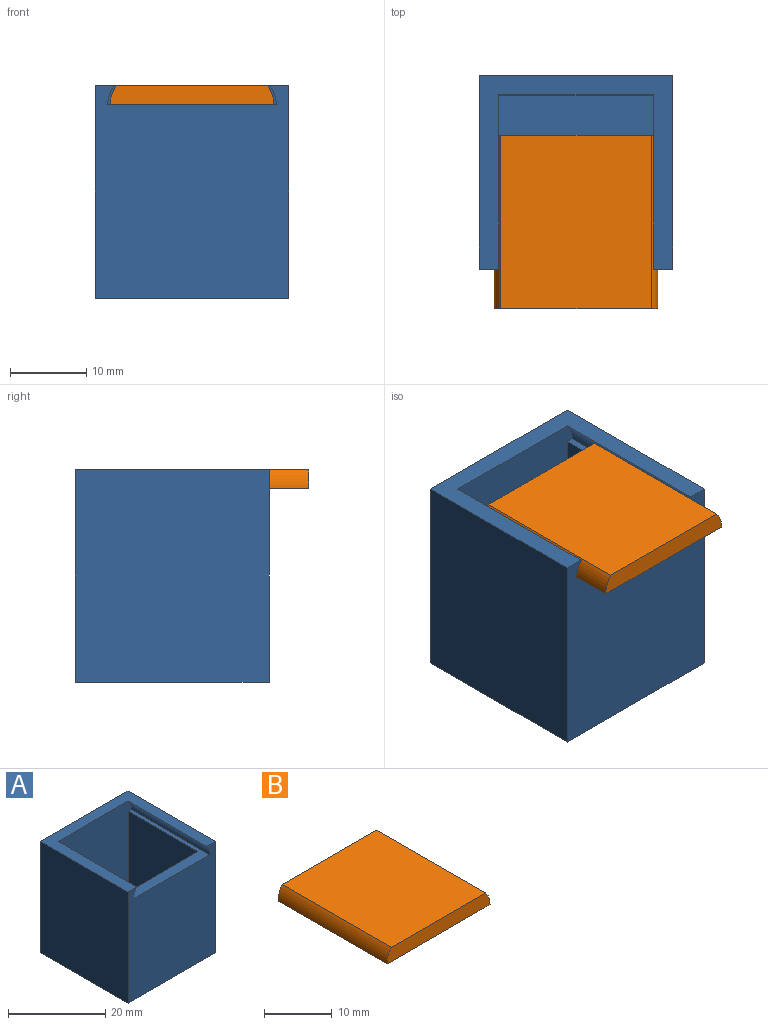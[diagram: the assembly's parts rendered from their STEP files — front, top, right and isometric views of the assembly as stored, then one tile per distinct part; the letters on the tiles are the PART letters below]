
ASSEMBLY  parts=2 mates=1
PART A: 14 faces, bbox 25.4x25.4x27.9 mm
  f0: plane 22.86x20.32mm, normal (-1,0,0), area 464.5mm2, adj f2,f9,f10,f11
  f1: plane 22.86x20.32mm, normal (1,0,0), area 464.5mm2, adj f2,f9,f10,f11
  f2: plane 22.86x20.32mm, normal (0,1,0), area 464.5mm2, adj f0,f1,f9,f11
  f3: plane 25.4x25.4mm, normal (0,0,1), area 180.6mm2, adj f5,f6,f7,f8,f10,f12,f13
  f4: plane 25.4x25.4mm, normal (0,0,-1), area 645.2mm2, adj f5,f6,f7,f8
  f5: plane 27.94x25.4mm, normal (1,0,0), area 709.7mm2, adj f3,f4,f7,f8
  f6: plane 27.94x25.4mm, normal (-1,0,0), area 709.7mm2, adj f3,f4,f7,f8
  f7: plane 27.94x25.4mm, normal (0,-1,0), area 655mm2, adj f3,f4,f5,f6,f11,f12,f13
  f8: plane 27.94x25.4mm, normal (0,1,0), area 709.7mm2, adj f3,f4,f5,f6
  f9: plane 20.32x20.32mm, normal (0,0,1), area 412.9mm2, adj f0,f1,f2,f10
  f10: plane 25.4x22.11mm, normal (0,-1,0), area 519.2mm2, adj f0,f1,f3,f9,f11,f12,f13
  f11: plane 22.86x22.11mm, normal (0,0,1), area 92.5mm2, adj f0,f1,f2,f7,f10,f12,f13
  f12: cylinder r=4.03mm len=22.86mm, axis (0,-1,0), area 62.8mm2, adj f3,f7,f10,f11
  f13: cylinder r=4.07mm len=22.86mm, axis (0,-1,0), area 62.7mm2, adj f3,f7,f10,f11
PART B: 6 faces, bbox 21.5x22.7x2.5 mm
  f0: plane 22.73x19.69mm, normal (0,0,1), area 447.5mm2, adj f1,f3,f4,f5
  f1: cylinder r=4.07mm len=22.73mm, axis (0,1,0), area 62.3mm2, adj f0,f2,f4,f5
  f2: plane 22.73x21.48mm, normal (0,0,-1), area 488.2mm2, adj f1,f3,f4,f5
  f3: cylinder r=4.03mm len=22.73mm, axis (0,1,0), area 62.5mm2, adj f0,f2,f4,f5
  f4: plane 21.48x2.54mm, normal (0,-1,0), area 53.1mm2, adj f0,f1,f2,f3
  f5: plane 21.48x2.54mm, normal (0,1,0), area 53.1mm2, adj f0,f1,f2,f3
PLACE A t=(-8.77,5.78,-2.79)mm fixed
PLACE B t=(-8.45,-13.43,9.93)mm
MATE slider B.f4 <-> A.f7  axis (0,-1,0) through (-8.76,-24.8,8.64)mm
